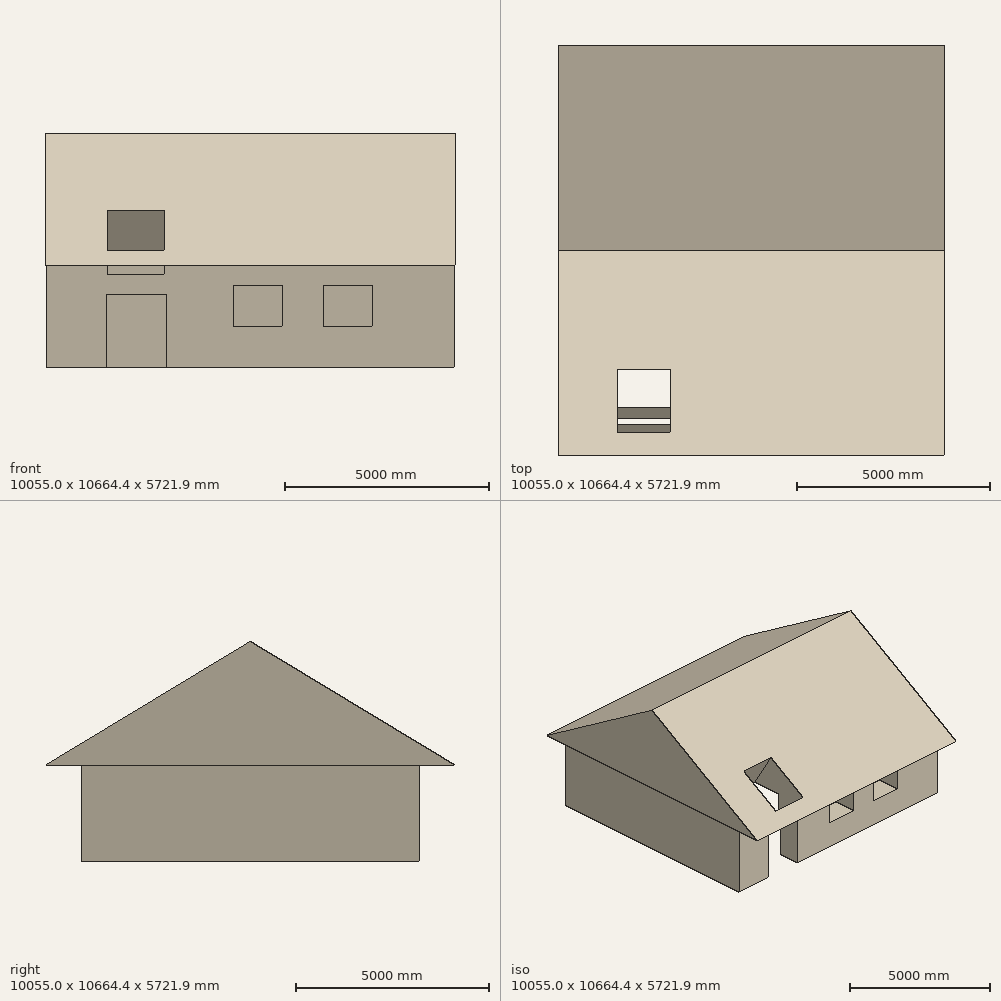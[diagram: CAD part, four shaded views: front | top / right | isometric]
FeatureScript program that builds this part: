
annotation { "Feature Type Name" : "Feature", "Feature Type Description" : "" }
export const myFeature = defineFeature(function(context is Context, id is Id, definition is map)
    precondition{}
    {
        {
            var Q0;
            Q0=qCreatedBy(makeId("Top.planeOp"),FACE);
            var sketch = newSketch(context, id + "F0", { "sketchPlane" : qUnion([Q0])});
            skLineSegment(sketch, "E0.bottom", {"start": v(-4999.32, 4387.69) * mm, "end": v(5000.68, 4387.69) * mm});
            skLineSegment(sketch, "E0.top", {"start": v(-4999.32, -4389.74) * mm, "end": v(5000.68, -4389.74) * mm});
            skLineSegment(sketch, "E0.left", {"start": v(-4999.32, 4387.69) * mm, "end": v(-4999.32, -4389.74) * mm});
            skLineSegment(sketch, "E0.right", {"start": v(5000.68, 4387.69) * mm, "end": v(5000.68, -4389.74) * mm});
            skLineSegment(sketch, "E1.bottom", {"start": v(-4027.53, 3572.64) * mm, "end": v(4122.94, 3572.64) * mm});
            skLineSegment(sketch, "E1.top", {"start": v(-4027.53, -3512) * mm, "end": v(4122.94, -3512) * mm});
            skLineSegment(sketch, "E1.left", {"start": v(-4027.53, 3572.64) * mm, "end": v(-4027.53, -3512) * mm});
            skLineSegment(sketch, "E1.right", {"start": v(4122.94, 3572.64) * mm, "end": v(4122.94, -3512) * mm});
            skSolve(sketch);
        }
        {
            var Q0;
            Q0 = qSketchRegion(id + "F0", true);
            extrude(context, id + "F1", {"entities" : qUnion([Q0]), "depth" : 2500 * mm, "offsetDistance" : 25 * mm});
        }
        {
            var Q0;
            Q0=makeQuery(id+"F1.opExtrude","SWEPT_FACE",FACE,{"disambiguationData":[OSD([sQuery(id+"F0.wireOp",EDGE,"E0.top")])]});
            var sketch = newSketch(context, id + "F2", { "sketchPlane" : qUnion([Q0])});
            skLineSegment(sketch, "E2.bottom", {"start": v(-3529.65, 1789.88) * mm, "end": v(-2059.29, 1789.88) * mm});
            skLineSegment(sketch, "E2.top", {"start": v(-3529.65, 0) * mm, "end": v(-2059.29, 0) * mm});
            skLineSegment(sketch, "E2.left", {"start": v(-3529.65, 1789.88) * mm, "end": v(-3529.65, 0) * mm});
            skLineSegment(sketch, "E2.right", {"start": v(-2059.29, 1789.88) * mm, "end": v(-2059.29, 0) * mm});
            skLineSegment(sketch, "E3.bottom", {"start": v(-422.66, 2000) * mm, "end": v(777.34, 2000) * mm});
            skLineSegment(sketch, "E3.top", {"start": v(-422.66, 1000) * mm, "end": v(777.34, 1000) * mm});
            skLineSegment(sketch, "E3.left", {"start": v(-422.66, 2000) * mm, "end": v(-422.66, 1000) * mm});
            skLineSegment(sketch, "E3.right", {"start": v(777.34, 2000) * mm, "end": v(777.34, 1000) * mm});
            skLineSegment(sketch, "E4.bottom", {"start": v(1795.43, 2000) * mm, "end": v(2995.43, 2000) * mm});
            skLineSegment(sketch, "E4.top", {"start": v(1795.43, 1000) * mm, "end": v(2995.43, 1000) * mm});
            skLineSegment(sketch, "E4.left", {"start": v(1795.43, 2000) * mm, "end": v(1795.43, 1000) * mm});
            skLineSegment(sketch, "E4.right", {"start": v(2995.43, 2000) * mm, "end": v(2995.43, 1000) * mm});
            skSolve(sketch);
        }
        {
            var Q0;
            Q0=makeQuery(id+"F2.imprint","IMPRINT",FACE,{"disambiguationData":[TD([[makeQuery(id+"F2.imprint","IMPRINT",EDGE,{"derivedFrom":sQuery(id+"F2.wireOp",EDGE,"E2.bottom")}),-1.0]])]});
            var Q1;
            Q1=makeQuery(id+"F2.imprint","IMPRINT",FACE,{"disambiguationData":[TD([[makeQuery(id+"F2.imprint","IMPRINT",EDGE,{"derivedFrom":sQuery(id+"F2.wireOp",EDGE,"E3.bottom")}),-1.0]])]});
            var Q2;
            Q2=makeQuery(id+"F2.imprint","IMPRINT",FACE,{"disambiguationData":[TD([[makeQuery(id+"F2.imprint","IMPRINT",EDGE,{"derivedFrom":sQuery(id+"F2.wireOp",EDGE,"E4.bottom")}),-1.0]])]});
            extrude(context, id + "F3", {"entities" : qUnion([Q0, Q1, Q2]), "operationType" : NewBodyOperationType.REMOVE, "endBound" : BoundingType.UP_TO_NEXT, "oppositeDirection" : true, "depth" : 25 * mm, "offsetDistance" : 25 * mm});
        }
        {
            var Q0;
            Q0=makeQuery(id+"F1.opExtrude","SWEPT_FACE",FACE,{"disambiguationData":[OSD([sQuery(id+"F0.wireOp",EDGE,"E0.left")])]});
            var sketch = newSketch(context, id + "F4", { "sketchPlane" : qUnion([Q0])});
            skLineSegment(sketch, "E5", {"start": v(-4374.62, 2500) * mm, "end": v(-5324.62, 2500) * mm});
            skLineSegment(sketch, "E6", {"start": v(-5324.62, 2500) * mm, "end": v(7.56, 5721.92) * mm});
            skLineSegment(sketch, "E7", {"start": v(7.56, 5721.92) * mm, "end": v(5339.74, 2500) * mm});
            skLineSegment(sketch, "E8", {"start": v(5339.74, 2500) * mm, "end": v(4389.74, 2500) * mm});
            skSolve(sketch);
        }
        {
            var Q0;
            {var subQ0=sQuery(id+"F4.wireOp",EDGE,"E6");Q0=makeQuery(id+"F4.imprint","IMPRINT",FACE,{"disambiguationData":[TD([[makeQuery(id+"F4.imprint","IMPRINT",EDGE,{"derivedFrom":subQ0}),-1.0]])]});}
            extrude(context, id + "F5", {"entities" : qUnion([Q0]), "operationType" : NewBodyOperationType.ADD, "oppositeDirection" : true, "depth" : 10030 * mm, "offsetDistance" : 25 * mm, "hasSecondDirection" : true, "secondDirectionOppositeDirection" : false, "secondDirectionDepth" : 25 * mm});
        }
        {
            var Q0;
            Q0=makeQuery(id+"F5.opExtrude","SWEPT_FACE",FACE,{"disambiguationData":[OSD([sQuery(id+"F4.wireOp",EDGE,"E7")])]});
            var sketch = newSketch(context, id + "F6", { "sketchPlane" : qUnion([Q0])});
            skLineSegment(sketch, "E9.bottom", {"start": v(-3492.81, -677.31) * mm, "end": v(-2112.81, -677.31) * mm});
            skLineSegment(sketch, "E9.top", {"start": v(-3492.81, -2577.31) * mm, "end": v(-2112.81, -2577.31) * mm});
            skLineSegment(sketch, "E9.left", {"start": v(-3492.81, -677.31) * mm, "end": v(-3492.81, -2577.31) * mm});
            skLineSegment(sketch, "E9.right", {"start": v(-2112.81, -677.31) * mm, "end": v(-2112.81, -2577.31) * mm});
            skSolve(sketch);
        }
        {
            var Q0;
            Q0 = qSketchRegion(id + "F6", true);
            extrude(context, id + "F7", {"entities" : qUnion([Q0]), "operationType" : NewBodyOperationType.REMOVE, "endBound" : BoundingType.UP_TO_NEXT, "oppositeDirection" : true, "depth" : 25 * mm, "offsetDistance" : 25 * mm});
        }
    });
